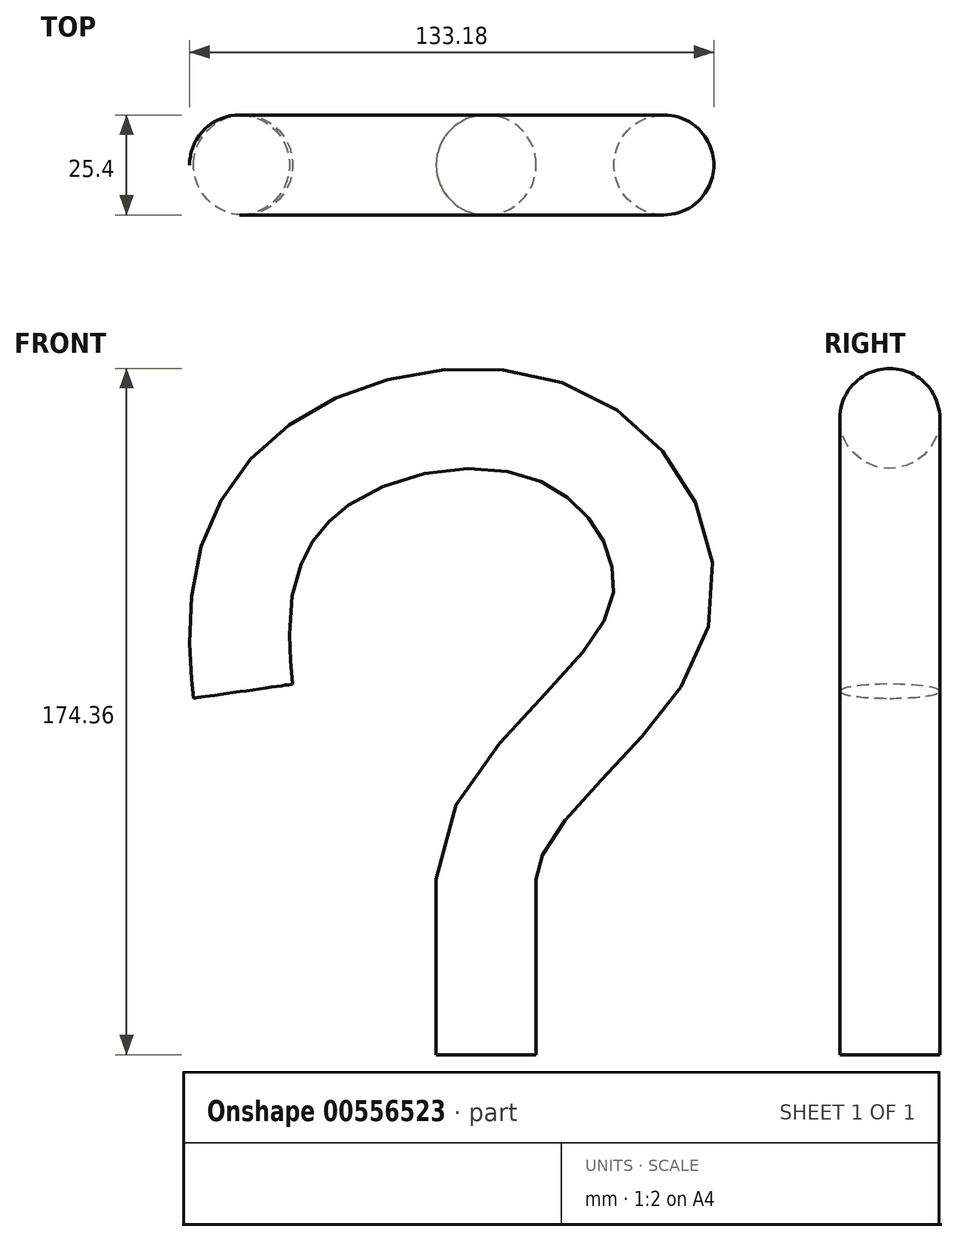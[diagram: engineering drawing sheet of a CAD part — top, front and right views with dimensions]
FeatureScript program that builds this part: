
annotation { "Feature Type Name" : "Feature", "Feature Type Description" : "" }
export const myFeature = defineFeature(function(context is Context, id is Id, definition is map)
    precondition{}
    {
        {
            var Q0;
            Q0=qCreatedBy(makeId("Top.planeOp"),FACE);
            var sketch = newSketch(context, id + "F0", { "sketchPlane" : qUnion([Q0])});
            skCircle(sketch, "E0", {"center": v(0, 0) * mm, "radius": 12.7 * mm});
            skSolve(sketch);
        }
        {
            var Q0;
            Q0=qCreatedBy(makeId("Front.planeOp"),FACE);
            var sketch = newSketch(context, id + "F1", { "sketchPlane" : qUnion([Q0])});
            skLineSegment(sketch, "E1", {"start": v(0, 0) * mm, "end": v(0, 44.54) * mm});
            skFitSpline(sketch, "E2", {"points": [v(0, 44.54) * mm, v(43.17, 108.7) * mm, v(21.7, 155.9) * mm, v(-37.36, 153.04) * mm, v(-61.75, 118.87) * mm, v(-61.73, 92.35) * mm], "startDerivative": vector(0, 276.1) * mm, "endDerivative": vector(4.35, -30.52) * mm});
            skSolve(sketch);
        }
        {
            var Q0;
            Q0 = qSketchRegion(id + "F0", true);
            var Q1;
            Q1 = qConstructionFilter(qBodyType(qCreatedBy(id + "F1" ,EDGE), BodyType.WIRE), ConstructionObject.NO);
            sweep(context, id + "F2", {"profiles" : qUnion([Q0]), "path" : qUnion([Q1])});
        }
    });
